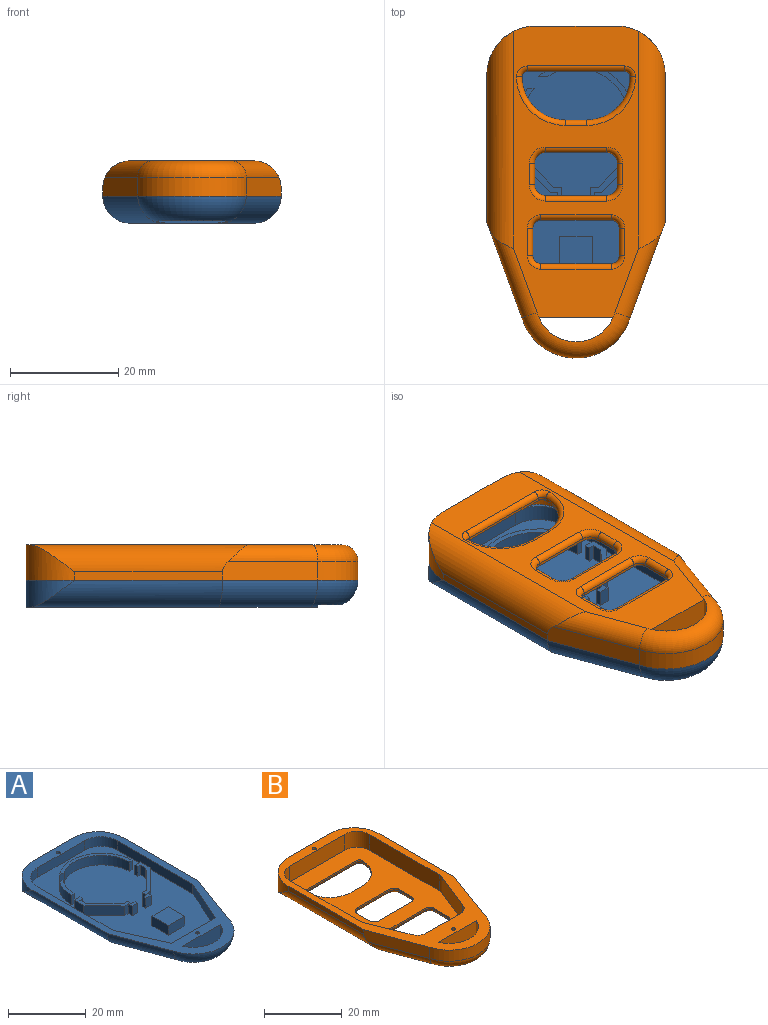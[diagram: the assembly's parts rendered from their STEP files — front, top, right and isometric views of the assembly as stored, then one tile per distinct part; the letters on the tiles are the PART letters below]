
ASSEMBLY  parts=2 mates=1
PART A: 72 faces, bbox 33.2x62.5x8.7 mm
  f0: cylinder r=7.47mm len=13.68mm, axis (0,0,-1), area 79.2mm2, adj f14,f15,f69
  f1: plane 14.9x5mm, normal (0,1,0), area 74.5mm2, adj f2,f12,f15,f16
  f2: cylinder r=9.05mm len=9.05mm, axis (0,0,-1), area 52.2mm2, adj f1,f15,f16,f67
  f3: cylinder r=6mm len=6mm, axis (0,0,-1), area 28.3mm2, adj f4,f13,f15,f36
  f4: plane 27.38x3mm, normal (-1,0,0), area 82.1mm2, adj f3,f5,f15,f36
  f5: plane 14.62x6.5mm, normal (-0.91,0.41,0), area 48mm2, adj f4,f6,f15,f36
  f6: plane 16x3mm, normal (0,1,0), area 48mm2, adj f5,f7,f15,f36
  f7: plane 14.62x6.5mm, normal (0.91,0.41,0), area 48mm2, adj f6,f8,f15,f36
  f8: plane 27.38x3mm, normal (1,0,0), area 82.1mm2, adj f7,f9,f15,f36
  f9: cylinder r=6mm len=6mm, axis (0,0,-1), area 28.3mm2, adj f8,f13,f15,f36
  f10: cylinder r=0.5mm len=4mm, axis (0,0,-1), area 12.6mm2, adj f15,f20
  f11: cylinder r=0.5mm len=4mm, axis (0,0,-1), area 12.6mm2, adj f15,f18
  f12: cylinder r=9.05mm len=9.05mm, axis (0,0,-1), area 52.2mm2, adj f1,f15,f16,f71
  f13: plane 17x3mm, normal (0,-1,0), area 51mm2, adj f3,f9,f15,f36
  f14: plane 13.87x5.19mm, normal (0,-1,0), area 67.8mm2, adj f0,f15,f16,f69
  f15: plane 61.47x33mm, normal (0,0,1), area 415.9mm2, adj f0,f1,f2,f3,f4,f5,f6,f7
  f16: plane 54x23mm, normal (0,0,-1), area 1107.3mm2, adj f1,f2,f12,f14,f17,f19,f67,f68
  f17: cylinder r=1mm len=2mm, axis (0,0,-1), area 6.3mm2, adj f16,f18
  f18: plane 2x2mm, normal (0,0,-1), area 2.4mm2, adj f11,f17
  f19: cylinder r=1mm len=2mm, axis (0,0,-1), area 6.3mm2, adj f16,f20
  f20: plane 2x2mm, normal (0,0,-1), area 2.4mm2, adj f10,f19
  f21: plane 3x2mm, normal (0,1,0), area 6mm2, adj f22,f34,f35,f36
  f22: plane 3x1mm, normal (-1,0,0), area 3mm2, adj f21,f23,f35,f36
  f23: plane 3x1mm, normal (0,-1,0), area 3mm2, adj f22,f24,f35,f36
  f24: plane 3x2mm, normal (-1,0,0), area 6mm2, adj f23,f25,f35,f36
  f25: plane 7x6.75mm, normal (-0.72,0.69,0), area 29.2mm2, adj f24,f26,f35,f36
  f26: plane 3x1.5mm, normal (0,1,0), area 4.5mm2, adj f25,f27,f35,f36
  f27: plane 3x1.5mm, normal (-1,0,0), area 4.5mm2, adj f26,f28,f35,f36
  f28: plane 3x1.35mm, normal (0,1,0), area 4.1mm2, adj f27,f29,f35,f36
  f29: plane 3x1mm, normal (-1,0,0), area 3mm2, adj f28,f30,f35,f36
  f30: plane 3x2mm, normal (0,-1,0), area 6mm2, adj f29,f31,f35,f36
  f31: plane 3x1.5mm, normal (1,0,0), area 4.5mm2, adj f30,f32,f35,f36
  f32: plane 3x1.37mm, normal (0,-1,0), area 4.1mm2, adj f31,f33,f35,f36
  f33: plane 7.5x7.23mm, normal (0.72,-0.69,0), area 31.3mm2, adj f32,f34,f35,f36
  f34: plane 3.5x3mm, normal (1,0,0), area 10.5mm2, adj f21,f33,f35,f36
  f35: plane 12.5x10.6mm, normal (0,0,1), area 19.1mm2, adj f21,f22,f23,f24,f25,f26,f27,f28
  f36: plane 48x29mm, normal (0,0,1), area 1177.5mm2, adj f3,f4,f5,f6,f7,f8,f9,f13
  f37: plane 3x1mm, normal (1,0,0), area 3mm2, adj f36,f38,f50,f51
  f38: plane 3x2mm, normal (0,1,0), area 6mm2, adj f36,f37,f39,f51
  f39: plane 3.5x3mm, normal (-1,0,0), area 10.5mm2, adj f36,f38,f40,f51
  f40: plane 7.5x7.23mm, normal (-0.72,-0.69,0), area 31.3mm2, adj f36,f39,f41,f51
  f41: plane 3x1.37mm, normal (0,-1,0), area 4.1mm2, adj f36,f40,f42,f51
  f42: plane 3x1.5mm, normal (-1,0,0), area 4.5mm2, adj f36,f41,f43,f51
  f43: plane 3x2mm, normal (0,-1,0), area 6mm2, adj f36,f42,f44,f51
  f44: plane 3x1mm, normal (1,0,0), area 3mm2, adj f36,f43,f45,f51
  f45: plane 3x1.35mm, normal (0,1,0), area 4.1mm2, adj f36,f44,f46,f51
  f46: plane 3x1.5mm, normal (1,0,0), area 4.5mm2, adj f36,f45,f47,f51
  f47: plane 3x1.5mm, normal (0,1,0), area 4.5mm2, adj f36,f46,f48,f51
  f48: plane 7x6.75mm, normal (0.72,0.69,0), area 29.2mm2, adj f36,f47,f49,f51
  f49: plane 3x2mm, normal (1,0,0), area 6mm2, adj f36,f48,f50,f51
  f50: plane 3x1mm, normal (0,-1,0), area 3mm2, adj f36,f37,f49,f51
  f51: plane 12.5x10.6mm, normal (0,0,1), area 19.1mm2, adj f37,f38,f39,f40,f41,f42,f43,f44
  f52: cylinder r=11mm len=17.97mm, axis (0,0,-1), area 74.5mm2, adj f36,f53,f55,f56
  f53: plane 3x1.73mm, normal (0,-1,0), area 5.2mm2, adj f36,f52,f54,f56
  f54: cylinder r=10mm len=15.24mm, axis (0,0,-1), area 63.7mm2, adj f36,f53,f55,f56
  f55: plane 3x1mm, normal (0,-1,0), area 3mm2, adj f36,f52,f54,f56
  f56: plane 17.97x11mm, normal (0,0,1), area 23.1mm2, adj f52,f53,f54,f55
  f57: cylinder r=10mm len=6.34mm, axis (0,0,-1), area 20.6mm2, adj f36,f58,f60,f61
  f58: plane 3x1.26mm, normal (0,1,0), area 3.8mm2, adj f36,f57,f59,f61
  f59: cylinder r=11mm len=6.33mm, axis (0,0,-1), area 20.2mm2, adj f36,f58,f60,f61
  f60: plane 3x1mm, normal (0,-1,0), area 3mm2, adj f36,f57,f59,f61
  f61: plane 6.34x3.26mm, normal (0,0,1), area 6.8mm2, adj f57,f58,f59,f60
  f62: plane 6x3mm, normal (0,1,0), area 18mm2, adj f36,f63,f65,f66
  f63: plane 6x3mm, normal (-1,0,0), area 18mm2, adj f36,f62,f64,f66
  f64: plane 6x3mm, normal (0,-1,0), area 18mm2, adj f36,f63,f65,f66
  f65: plane 6x3mm, normal (1,0,0), area 18mm2, adj f36,f62,f64,f66
  f66: plane 6x6mm, normal (0,0,1), area 36mm2, adj f62,f63,f64,f65
  f67: cylinder r=5mm len=35.42mm, axis (0,-1,0), area 248.5mm2, adj f2,f15,f16,f68
  f68: cylinder r=5mm len=19.51mm, axis (0.34,-0.94,0), area 145.6mm2, adj f15,f16,f67,f69
  f69: torus R=5.47mm, axis (0,0,1), area 146.6mm2, adj f0,f14,f15,f16,f68,f70
  f70: cylinder r=5mm len=19.51mm, axis (0.34,0.94,0), area 145.6mm2, adj f15,f16,f69,f71
  f71: cylinder r=5mm len=35.42mm, axis (0,1,0), area 248.5mm2, adj f12,f15,f16,f70
PART B: 78 faces, bbox 33x62.3x6.5 mm
  f0: cylinder r=7.47mm len=13.68mm, axis (0,0,-1), area 112.4mm2, adj f21,f22,f54
  f1: cylinder r=10.47mm len=20.06mm, axis (0,0,-1), area 93.8mm2, adj f2,f19,f22,f54
  f2: plane 17.62x6.47mm, normal (0.94,-0.34,0), area 64.9mm2, adj f1,f3,f22,f48,f53
  f3: plane 27.38x1.5mm, normal (1,0,0), area 41.1mm2, adj f2,f4,f22,f48
  f4: cylinder r=9.05mm len=9.05mm, axis (0,0,-1), area 73.4mm2, adj f3,f5,f22,f45,f48
  f5: plane 14.9x6.5mm, normal (0,1,0), area 96.9mm2, adj f4,f6,f22,f45
  f6: cylinder r=9.05mm len=9.05mm, axis (0,0,-1), area 73.4mm2, adj f5,f7,f22,f45,f47
  f7: plane 27.38x1.5mm, normal (-1,0,0), area 41.1mm2, adj f6,f19,f22,f47
  f8: plane 12.18x5mm, normal (0,1,0), area 60.9mm2, adj f9,f20,f22,f46
  f9: cylinder r=3.39mm len=5mm, axis (0,0,-1), area 20.4mm2, adj f8,f10,f22,f46
  f10: plane 12.59x5.04mm, normal (0.93,0.37,0), area 67.8mm2, adj f9,f11,f22,f46
  f11: cylinder r=3mm len=5mm, axis (0,0,-1), area 6.7mm2, adj f10,f12,f22,f46
  f12: plane 25.33x5mm, normal (1,0,0), area 126.7mm2, adj f11,f13,f22,f46
  f13: cylinder r=4.5mm len=5mm, axis (0,0,-1), area 35.3mm2, adj f12,f14,f22,f46
  f14: plane 20x5mm, normal (0,-1,0), area 100mm2, adj f13,f15,f22,f46
  f15: cylinder r=4.5mm len=5mm, axis (0,0,-1), area 35.3mm2, adj f14,f16,f22,f46
  f16: plane 25.33x5mm, normal (-1,0,0), area 126.7mm2, adj f15,f17,f22,f46
  f17: cylinder r=3mm len=5mm, axis (0,0,-1), area 6.7mm2, adj f16,f18,f22,f46
  f18: plane 12.59x5.04mm, normal (-0.93,0.37,0), area 67.8mm2, adj f17,f20,f22,f46
  f19: plane 17.62x6.47mm, normal (-0.94,-0.34,0), area 64.9mm2, adj f1,f7,f22,f47,f55
  f20: cylinder r=3.39mm len=5mm, axis (0,0,-1), area 20.4mm2, adj f8,f18,f22,f46
  f21: plane 13.68x6.5mm, normal (0,-1,0), area 88.9mm2, adj f0,f22,f45
  f22: plane 61.47x33mm, normal (0,0,1), area 470.1mm2, adj f0,f1,f2,f3,f4,f5,f6,f7
  f23: cylinder r=1mm len=1mm, axis (0,0,1), area 0.8mm2, adj f24,f42,f46,f75
  f24: plane 18x0.5mm, normal (0,-1,0), area 9mm2, adj f23,f25,f46,f77
  f25: cylinder r=1mm len=1mm, axis (0,0,1), area 0.8mm2, adj f24,f26,f46,f76
  f26: cylinder r=8mm len=8mm, axis (0,0,1), area 6.3mm2, adj f25,f27,f46,f74
  f27: plane 4x0.5mm, normal (0,1,0), area 2mm2, adj f26,f42,f46,f72
  f28: cylinder r=2mm len=2mm, axis (0,0,1), area 1.6mm2, adj f29,f43,f46,f58
  f29: plane 4x0.5mm, normal (-1,0,0), area 2mm2, adj f28,f30,f46,f60
  f30: cylinder r=2mm len=2mm, axis (0,0,1), area 1.6mm2, adj f29,f31,f46,f62
  f31: plane 11.3x0.5mm, normal (0,1,0), area 5.6mm2, adj f30,f32,f46,f63
  f32: cylinder r=2mm len=2mm, axis (0,0,1), area 1.6mm2, adj f31,f33,f46,f61
  f33: plane 4x0.5mm, normal (1,0,0), area 2mm2, adj f32,f34,f46,f59
  f34: cylinder r=2mm len=2mm, axis (0,0,1), area 1.6mm2, adj f33,f43,f46,f57
  f35: cylinder r=1.5mm len=1.5mm, axis (0,0,1), area 1.2mm2, adj f36,f44,f46,f66
  f36: plane 5.1x0.5mm, normal (-1,0,0), area 2.6mm2, adj f35,f37,f46,f68
  f37: cylinder r=1.5mm len=1.5mm, axis (0,0,1), area 1.2mm2, adj f36,f38,f46,f70
  f38: plane 13x0.5mm, normal (0,1,0), area 6.5mm2, adj f37,f39,f46,f71
  f39: cylinder r=1.5mm len=1.5mm, axis (0,0,1), area 1.2mm2, adj f38,f40,f46,f69
  f40: plane 5.1x0.5mm, normal (1,0,0), area 2.6mm2, adj f39,f41,f46,f67
  f41: cylinder r=1.5mm len=1.5mm, axis (0,0,1), area 1.2mm2, adj f40,f44,f46,f65
  f42: cylinder r=8mm len=8mm, axis (0,0,1), area 6.3mm2, adj f23,f27,f46,f73
  f43: plane 11.3x0.5mm, normal (0,-1,0), area 5.6mm2, adj f28,f34,f46,f56
  f44: plane 13x0.5mm, normal (0,-1,0), area 6.5mm2, adj f35,f41,f46,f64
  f45: plane 54x23mm, normal (0,0,-1), area 633mm2, adj f4,f5,f6,f21,f47,f48,f53,f54
  f46: plane 45.91x29.01mm, normal (0,0,1), area 828.6mm2, adj f8,f9,f10,f11,f12,f13,f14,f15
  f47: cylinder r=5mm len=40.34mm, axis (0,-1,0), area 270.9mm2, adj f6,f7,f19,f45,f55
  f48: cylinder r=5mm len=40.34mm, axis (0,1,0), area 270.9mm2, adj f2,f3,f4,f45,f53
  f49: cylinder r=0.5mm len=1mm, axis (0,0,1), area 3.1mm2, adj f22,f50
  f50: plane 1x1mm, normal (0,0,1), area 0.8mm2, adj f49
  f51: cylinder r=0.5mm len=1mm, axis (0,0,1), area 3.1mm2, adj f22,f52
  f52: plane 1x1mm, normal (0,0,1), area 0.8mm2, adj f51
  f53: cylinder r=3mm len=17.61mm, axis (0.34,0.94,0), area 70.9mm2, adj f2,f45,f48,f54
  f54: torus R=7.47mm, axis (0,0,1), area 113.6mm2, adj f0,f1,f45,f53,f55
  f55: cylinder r=3mm len=17.61mm, axis (0.34,-0.94,0), area 70.9mm2, adj f19,f45,f47,f54
  f56: cylinder r=1mm len=11.3mm, axis (-1,0,0), area 17.7mm2, adj f43,f45,f57,f58
  f57: torus R=3mm, axis (0,0,1), area 5.8mm2, adj f34,f45,f56,f59
  f58: torus R=3mm, axis (0,0,1), area 5.8mm2, adj f28,f45,f56,f60
  f59: cylinder r=1mm len=4mm, axis (0,-1,0), area 6.3mm2, adj f33,f45,f57,f61
  f60: cylinder r=1mm len=4mm, axis (0,1,0), area 6.3mm2, adj f29,f45,f58,f62
  f61: torus R=3mm, axis (0,0,1), area 5.8mm2, adj f32,f45,f59,f63
  f62: torus R=3mm, axis (0,0,1), area 5.8mm2, adj f30,f45,f60,f63
  f63: cylinder r=1mm len=11.3mm, axis (1,0,0), area 17.7mm2, adj f31,f45,f61,f62
  f64: cylinder r=1mm len=13mm, axis (-1,0,0), area 20.4mm2, adj f44,f45,f65,f66
  f65: torus R=2.5mm, axis (0,0,1), area 4.6mm2, adj f41,f45,f64,f67
  f66: torus R=2.5mm, axis (0,0,1), area 4.6mm2, adj f35,f45,f64,f68
  f67: cylinder r=1mm len=5.1mm, axis (0,-1,0), area 8mm2, adj f40,f45,f65,f69
  f68: cylinder r=1mm len=5.1mm, axis (0,1,0), area 8mm2, adj f36,f45,f66,f70
  f69: torus R=2.5mm, axis (0,0,1), area 4.6mm2, adj f39,f45,f67,f71
  f70: torus R=2.5mm, axis (0,0,1), area 4.6mm2, adj f37,f45,f68,f71
  f71: cylinder r=1mm len=13mm, axis (1,0,0), area 20.4mm2, adj f38,f45,f69,f70
  f72: cylinder r=1mm len=4mm, axis (1,0,0), area 6.3mm2, adj f27,f45,f73,f74
  f73: torus R=9mm, axis (0,0,1), area 20.6mm2, adj f42,f45,f72,f75
  f74: torus R=9mm, axis (0,0,1), area 20.6mm2, adj f26,f45,f72,f76
  f75: torus R=2mm, axis (0,0,1), area 3.4mm2, adj f23,f45,f73,f77
  f76: torus R=2mm, axis (0,0,1), area 3.4mm2, adj f25,f45,f74,f77
  f77: cylinder r=1mm len=18mm, axis (-1,0,0), area 28.3mm2, adj f24,f45,f75,f76
PLACE A t=(-21.12,-37.72,-23.72)mm
PLACE B rot(axis=(0,1,0),180deg) t=(39,-37.95,-15.72)mm
MATE planar B.f22 <-> A.f15  axis (0,0,-1) through (-23.1,-12.33,-20.72)mm
